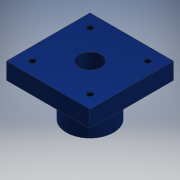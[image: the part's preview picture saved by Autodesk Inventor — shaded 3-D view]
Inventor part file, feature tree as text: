
AUTODESK INVENTOR PART (.ipt)
format: ipt  version: 2018 (Build 220112000, 112)  size: 128,000 bytes
history: native  units: mm
features: sketch x4, extrude x2, hole x2, other x1
ambient origin geometry x8: Origin, YZ Plane, XZ Plane, XY Plane, X Axis, Y Axis, Z Axis, Center Point
bodies: Body1 (feature_tree)
feature tree (9):
  other  "Sólido1"
  extrude  "Extrusión1"  Depth=45.0mm
  hole  "Agujero1"  [1 undecoded]
  hole  "Agujero2"  [1 undecoded]
  extrude  "Extrusión2"  Depth=18.0mm
  sketch  "Boceto1"  dims[d0=45.0mm d1=45.0mm]
  sketch  "Boceto2"  dims[d2=9.0mm d3=0.0mm d4=12.0mm]
  sketch  "Boceto3"  dims[d5=12.0mm d6=6.0mm d7=4.0mm d8=2.0mm d9=90.0deg d10=9.0mm d11=0.0mm d12=31.0mm]
  sketch  "Boceto4"  dims[d13=31.0mm d14=3.0mm d15=6.0mm d16=4.0mm d17=2.0mm d18=90.0deg d19=9.0mm d20=20.594885mm d21=25.4mm d22=18.0mm d23=0.0mm]
note: 2 required parameter values undecoded (feature->parameter linkage not recoverable at this tier; creation-order binding heuristic only, values carry confidence <= 0.55)
